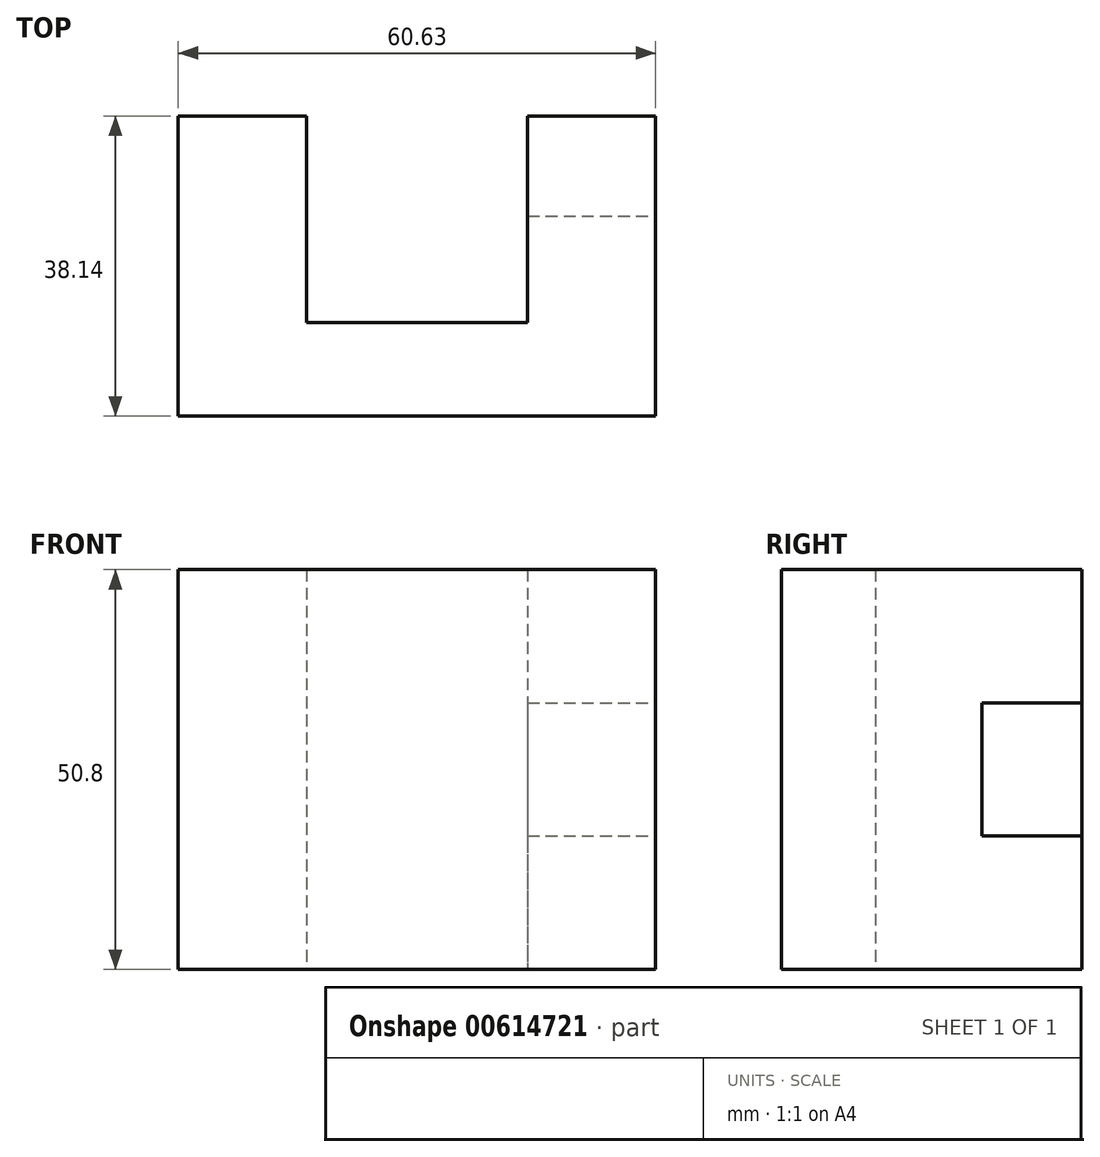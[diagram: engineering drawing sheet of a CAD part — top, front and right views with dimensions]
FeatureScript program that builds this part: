
annotation { "Feature Type Name" : "Feature", "Feature Type Description" : "" }
export const myFeature = defineFeature(function(context is Context, id is Id, definition is map)
    precondition{}
    {
        {
            var Q0;
            Q0=qCreatedBy(makeId("Top.planeOp"),FACE);
            var sketch = newSketch(context, id + "F0", { "sketchPlane" : qUnion([Q0])});
            skLineSegment(sketch, "E0.bottom", {"start": v(0, 0) * mm, "end": v(16.27, 0) * mm});
            skLineSegment(sketch, "E0.top", {"start": v(0, -38.14) * mm, "end": v(60.63, -38.14) * mm});
            skLineSegment(sketch, "E0.left", {"start": v(0, 0) * mm, "end": v(0, -38.14) * mm});
            skLineSegment(sketch, "E0.right", {"start": v(60.63, 0) * mm, "end": v(60.63, -38.14) * mm});
            skLineSegment(sketch, "E1.top", {"start": v(16.27, -26.23) * mm, "end": v(44.36, -26.23) * mm});
            skLineSegment(sketch, "E1.left", {"start": v(16.27, 0) * mm, "end": v(16.27, -26.23) * mm});
            skLineSegment(sketch, "E1.right", {"start": v(44.36, 0) * mm, "end": v(44.36, -26.23) * mm});
            skLineSegment(sketch, "E2.trimOffspring", {"start": v(44.36, 0) * mm, "end": v(60.63, 0) * mm});
            skSolve(sketch);
        }
        {
            var Q0;
            Q0 = qSketchRegion(id + "F0", true);
            extrude(context, id + "F1", {"entities" : qUnion([Q0]), "depth" : 50.8 * mm, "offsetDistance" : 25.4 * mm});
        }
        {
            var Q0;
            Q0=makeQuery(id+"F1.opExtrude","SWEPT_FACE",FACE,{"disambiguationData":[OSD([sQuery(id+"F0.wireOp",EDGE,"E2.trimOffspring")])]});
            var sketch = newSketch(context, id + "F2", { "sketchPlane" : qUnion([Q0])});
            skLineSegment(sketch, "E3.bottom", {"start": v(-44.36, 33.85) * mm, "end": v(-60.63, 33.85) * mm});
            skLineSegment(sketch, "E3.top", {"start": v(-44.36, 16.96) * mm, "end": v(-60.63, 16.96) * mm});
            skLineSegment(sketch, "E3.left", {"start": v(-44.36, 33.85) * mm, "end": v(-44.36, 16.96) * mm});
            skLineSegment(sketch, "E3.right", {"start": v(-60.63, 33.85) * mm, "end": v(-60.63, 16.96) * mm});
            skSolve(sketch);
        }
        {
            var Q0;
            Q0=makeQuery(id+"F2.imprint","IMPRINT",FACE,{"disambiguationData":[TD([[makeQuery(id+"F2.imprint","IMPRINT",EDGE,{"derivedFrom":sQuery(id+"F2.wireOp",EDGE,"E3.bottom")}),1.0]])]});
            extrude(context, id + "F3", {"entities" : qUnion([Q0]), "operationType" : NewBodyOperationType.REMOVE, "oppositeDirection" : true, "depth" : 12.7 * mm, "offsetDistance" : 25.4 * mm});
        }
    });
